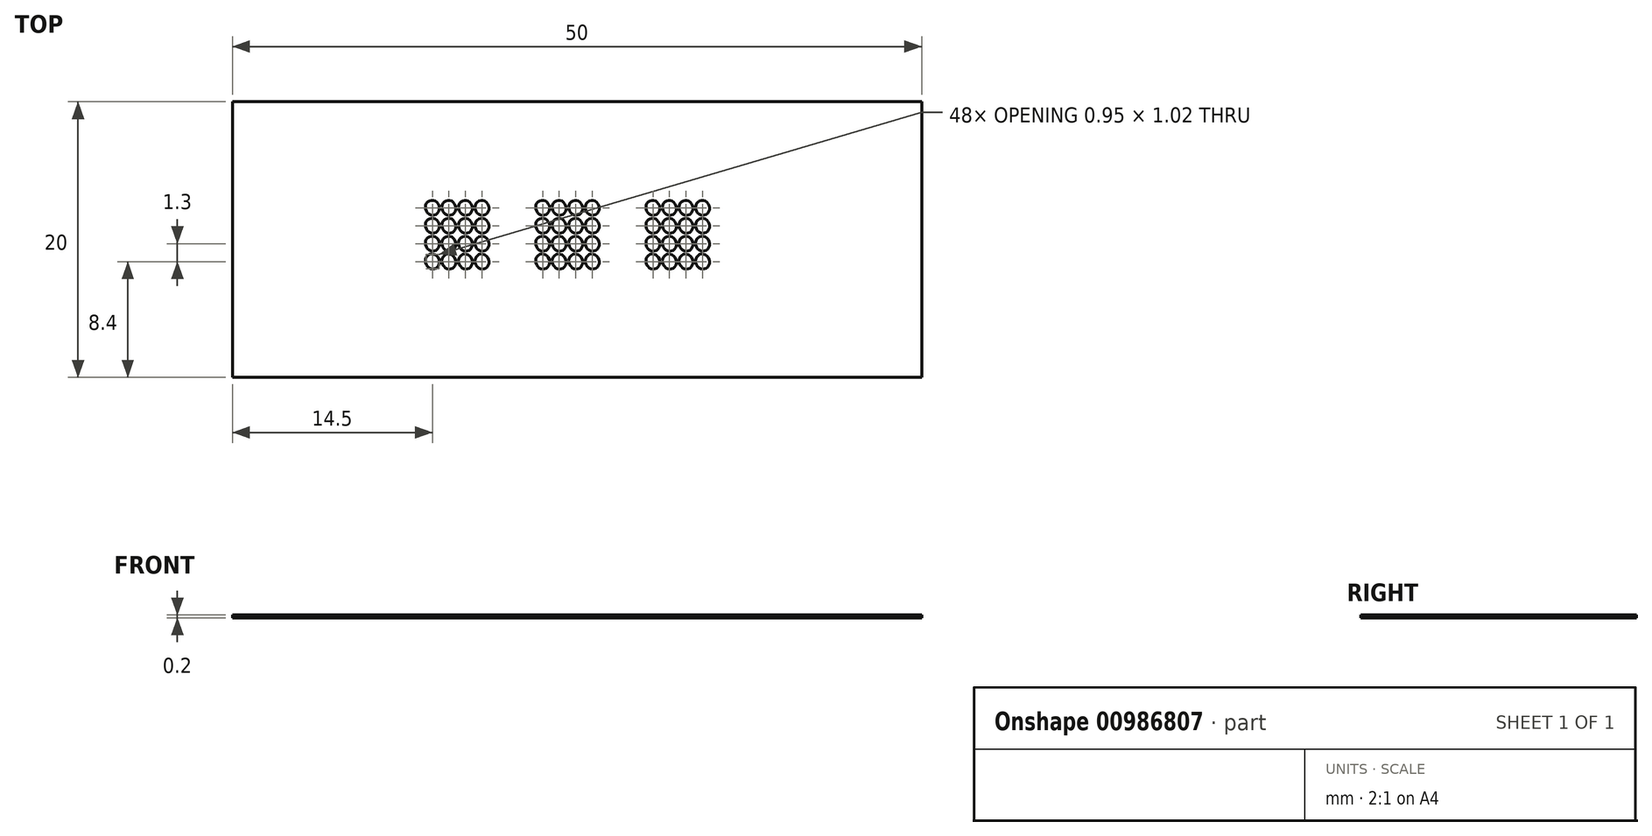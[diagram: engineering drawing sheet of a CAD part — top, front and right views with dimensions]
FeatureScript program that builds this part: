
annotation { "Feature Type Name" : "Feature", "Feature Type Description" : "" }
export const myFeature = defineFeature(function(context is Context, id is Id, definition is map)
    precondition{}
    {
        {
            var Q0;
            Q0=qCreatedBy(makeId("Top.planeOp"),FACE);
            var sketch = newSketch(context, id + "F0", { "sketchPlane" : qUnion([Q0])});
            skLineSegment(sketch, "E0.bottom", {"start": v(0, 0) * mm, "end": v(50, 0) * mm});
            skLineSegment(sketch, "E0.top", {"start": v(0, -20) * mm, "end": v(50, -20) * mm});
            skLineSegment(sketch, "E0.left", {"start": v(0, 0) * mm, "end": v(0, -20) * mm});
            skLineSegment(sketch, "E0.right", {"start": v(50, 0) * mm, "end": v(50, -20) * mm});
            skEllipse(sketch, "E1", {"center": v(14.5, -7.7) * mm, "majorRadius": 0.5 * mm, "minorRadius": 0.55 * mm, "majorAxis": v(0.93, 0.38)});
            skLineSegment(sketch, "E2.direction1", {"start": v(14.5, -7.7) * mm, "end": v(15.7, -7.7) * mm, "construction": true});
            skEllipse(sketch, "E3.0.1.0", {"center": v(15.7, -7.7) * mm, "majorRadius": 0.5 * mm, "minorRadius": 0.55 * mm, "majorAxis": v(0.93, 0.38)});
            skEllipse(sketch, "E3.0.2.0", {"center": v(16.9, -7.7) * mm, "majorRadius": 0.5 * mm, "minorRadius": 0.55 * mm, "majorAxis": v(0.93, 0.38)});
            skEllipse(sketch, "E3.0.3.0", {"center": v(18.1, -7.7) * mm, "majorRadius": 0.5 * mm, "minorRadius": 0.55 * mm, "majorAxis": v(0.93, 0.38)});
            skEllipse(sketch, "E4.1.0.0", {"center": v(15.7, -9) * mm, "majorRadius": 0.5 * mm, "minorRadius": 0.55 * mm, "majorAxis": v(0.93, 0.38)});
            skEllipse(sketch, "E4.1.0.1", {"center": v(14.5, -9) * mm, "majorRadius": 0.5 * mm, "minorRadius": 0.55 * mm, "majorAxis": v(0.93, 0.38)});
            skEllipse(sketch, "E4.1.0.2", {"center": v(18.1, -9) * mm, "majorRadius": 0.5 * mm, "minorRadius": 0.55 * mm, "majorAxis": v(0.93, 0.38)});
            skLineSegment(sketch, "E4.1.0.3", {"start": v(14.5, -9) * mm, "end": v(15.7, -9) * mm, "construction": true});
            skEllipse(sketch, "E4.1.0.4", {"center": v(16.9, -9) * mm, "majorRadius": 0.5 * mm, "minorRadius": 0.55 * mm, "majorAxis": v(0.93, 0.38)});
            skEllipse(sketch, "E4.2.0.0", {"center": v(15.7, -10.3) * mm, "majorRadius": 0.5 * mm, "minorRadius": 0.55 * mm, "majorAxis": v(0.93, 0.38)});
            skEllipse(sketch, "E4.2.0.1", {"center": v(14.5, -10.3) * mm, "majorRadius": 0.5 * mm, "minorRadius": 0.55 * mm, "majorAxis": v(0.93, 0.38)});
            skEllipse(sketch, "E4.2.0.2", {"center": v(18.1, -10.3) * mm, "majorRadius": 0.5 * mm, "minorRadius": 0.55 * mm, "majorAxis": v(0.93, 0.38)});
            skLineSegment(sketch, "E4.2.0.3", {"start": v(14.5, -10.3) * mm, "end": v(15.7, -10.3) * mm, "construction": true});
            skEllipse(sketch, "E4.2.0.4", {"center": v(16.9, -10.3) * mm, "majorRadius": 0.5 * mm, "minorRadius": 0.55 * mm, "majorAxis": v(0.93, 0.38)});
            skEllipse(sketch, "E4.3.0.0", {"center": v(15.7, -11.6) * mm, "majorRadius": 0.5 * mm, "minorRadius": 0.55 * mm, "majorAxis": v(0.93, 0.38)});
            skEllipse(sketch, "E4.3.0.1", {"center": v(14.5, -11.6) * mm, "majorRadius": 0.5 * mm, "minorRadius": 0.55 * mm, "majorAxis": v(0.93, 0.38)});
            skEllipse(sketch, "E4.3.0.2", {"center": v(18.1, -11.6) * mm, "majorRadius": 0.5 * mm, "minorRadius": 0.55 * mm, "majorAxis": v(0.93, 0.38)});
            skLineSegment(sketch, "E4.3.0.3", {"start": v(14.5, -11.6) * mm, "end": v(15.7, -11.6) * mm, "construction": true});
            skEllipse(sketch, "E4.3.0.4", {"center": v(16.9, -11.6) * mm, "majorRadius": 0.5 * mm, "minorRadius": 0.55 * mm, "majorAxis": v(0.93, 0.38)});
            skLineSegment(sketch, "E4.direction1", {"start": v(14.5, -7.7) * mm, "end": v(14.5, -9) * mm, "construction": true});
            skEllipse(sketch, "E5.1.0.0", {"center": v(22.5, -7.7) * mm, "majorRadius": 0.5 * mm, "minorRadius": 0.55 * mm, "majorAxis": v(0.93, 0.38)});
            skEllipse(sketch, "E5.1.0.1", {"center": v(24.9, -11.6) * mm, "majorRadius": 0.5 * mm, "minorRadius": 0.55 * mm, "majorAxis": v(0.93, 0.38)});
            skEllipse(sketch, "E5.1.0.2", {"center": v(23.7, -11.6) * mm, "majorRadius": 0.5 * mm, "minorRadius": 0.55 * mm, "majorAxis": v(0.93, 0.38)});
            skEllipse(sketch, "E5.1.0.3", {"center": v(22.5, -10.3) * mm, "majorRadius": 0.5 * mm, "minorRadius": 0.55 * mm, "majorAxis": v(0.93, 0.38)});
            skEllipse(sketch, "E5.1.0.4", {"center": v(22.5, -9) * mm, "majorRadius": 0.5 * mm, "minorRadius": 0.55 * mm, "majorAxis": v(0.93, 0.38)});
            skEllipse(sketch, "E5.1.0.5", {"center": v(22.5, -11.6) * mm, "majorRadius": 0.5 * mm, "minorRadius": 0.55 * mm, "majorAxis": v(0.93, 0.38)});
            skEllipse(sketch, "E5.1.0.6", {"center": v(26.1, -11.6) * mm, "majorRadius": 0.5 * mm, "minorRadius": 0.55 * mm, "majorAxis": v(0.93, 0.38)});
            skEllipse(sketch, "E5.1.0.7", {"center": v(26.1, -7.7) * mm, "majorRadius": 0.5 * mm, "minorRadius": 0.55 * mm, "majorAxis": v(0.93, 0.38)});
            skEllipse(sketch, "E5.1.0.8", {"center": v(24.9, -7.7) * mm, "majorRadius": 0.5 * mm, "minorRadius": 0.55 * mm, "majorAxis": v(0.93, 0.38)});
            skEllipse(sketch, "E5.1.0.9", {"center": v(26.1, -10.3) * mm, "majorRadius": 0.5 * mm, "minorRadius": 0.55 * mm, "majorAxis": v(0.93, 0.38)});
            skEllipse(sketch, "E5.1.0.10", {"center": v(24.9, -10.3) * mm, "majorRadius": 0.5 * mm, "minorRadius": 0.55 * mm, "majorAxis": v(0.93, 0.38)});
            skEllipse(sketch, "E5.1.0.11", {"center": v(26.1, -9) * mm, "majorRadius": 0.5 * mm, "minorRadius": 0.55 * mm, "majorAxis": v(0.93, 0.38)});
            skEllipse(sketch, "E5.1.0.12", {"center": v(24.9, -9) * mm, "majorRadius": 0.5 * mm, "minorRadius": 0.55 * mm, "majorAxis": v(0.93, 0.38)});
            skEllipse(sketch, "E5.1.0.13", {"center": v(23.7, -9) * mm, "majorRadius": 0.5 * mm, "minorRadius": 0.55 * mm, "majorAxis": v(0.93, 0.38)});
            skLineSegment(sketch, "E5.1.0.14", {"start": v(22.5, -7.7) * mm, "end": v(23.7, -7.7) * mm, "construction": true});
            skEllipse(sketch, "E5.1.0.15", {"center": v(23.7, -7.7) * mm, "majorRadius": 0.5 * mm, "minorRadius": 0.55 * mm, "majorAxis": v(0.93, 0.38)});
            skEllipse(sketch, "E5.1.0.16", {"center": v(23.7, -10.3) * mm, "majorRadius": 0.5 * mm, "minorRadius": 0.55 * mm, "majorAxis": v(0.93, 0.38)});
            skLineSegment(sketch, "E5.1.0.17", {"start": v(22.5, -9) * mm, "end": v(23.7, -9) * mm, "construction": true});
            skLineSegment(sketch, "E5.1.0.18", {"start": v(22.5, -11.6) * mm, "end": v(23.7, -11.6) * mm, "construction": true});
            skLineSegment(sketch, "E5.1.0.19", {"start": v(22.5, -10.3) * mm, "end": v(23.7, -10.3) * mm, "construction": true});
            skLineSegment(sketch, "E5.1.0.20", {"start": v(22.5, -7.7) * mm, "end": v(22.5, -9) * mm, "construction": true});
            skEllipse(sketch, "E5.2.0.0", {"center": v(30.5, -7.7) * mm, "majorRadius": 0.5 * mm, "minorRadius": 0.55 * mm, "majorAxis": v(0.93, 0.38)});
            skEllipse(sketch, "E5.2.0.1", {"center": v(32.9, -11.6) * mm, "majorRadius": 0.5 * mm, "minorRadius": 0.55 * mm, "majorAxis": v(0.93, 0.38)});
            skEllipse(sketch, "E5.2.0.2", {"center": v(31.7, -11.6) * mm, "majorRadius": 0.5 * mm, "minorRadius": 0.55 * mm, "majorAxis": v(0.93, 0.38)});
            skEllipse(sketch, "E5.2.0.3", {"center": v(30.5, -10.3) * mm, "majorRadius": 0.5 * mm, "minorRadius": 0.55 * mm, "majorAxis": v(0.93, 0.38)});
            skEllipse(sketch, "E5.2.0.4", {"center": v(30.5, -9) * mm, "majorRadius": 0.5 * mm, "minorRadius": 0.55 * mm, "majorAxis": v(0.93, 0.38)});
            skEllipse(sketch, "E5.2.0.5", {"center": v(30.5, -11.6) * mm, "majorRadius": 0.5 * mm, "minorRadius": 0.55 * mm, "majorAxis": v(0.93, 0.38)});
            skEllipse(sketch, "E5.2.0.6", {"center": v(34.1, -11.6) * mm, "majorRadius": 0.5 * mm, "minorRadius": 0.55 * mm, "majorAxis": v(0.93, 0.38)});
            skEllipse(sketch, "E5.2.0.7", {"center": v(34.1, -7.7) * mm, "majorRadius": 0.5 * mm, "minorRadius": 0.55 * mm, "majorAxis": v(0.93, 0.38)});
            skEllipse(sketch, "E5.2.0.8", {"center": v(32.9, -7.7) * mm, "majorRadius": 0.5 * mm, "minorRadius": 0.55 * mm, "majorAxis": v(0.93, 0.38)});
            skEllipse(sketch, "E5.2.0.9", {"center": v(34.1, -10.3) * mm, "majorRadius": 0.5 * mm, "minorRadius": 0.55 * mm, "majorAxis": v(0.93, 0.38)});
            skEllipse(sketch, "E5.2.0.10", {"center": v(32.9, -10.3) * mm, "majorRadius": 0.5 * mm, "minorRadius": 0.55 * mm, "majorAxis": v(0.93, 0.38)});
            skEllipse(sketch, "E5.2.0.11", {"center": v(34.1, -9) * mm, "majorRadius": 0.5 * mm, "minorRadius": 0.55 * mm, "majorAxis": v(0.93, 0.38)});
            skEllipse(sketch, "E5.2.0.12", {"center": v(32.9, -9) * mm, "majorRadius": 0.5 * mm, "minorRadius": 0.55 * mm, "majorAxis": v(0.93, 0.38)});
            skEllipse(sketch, "E5.2.0.13", {"center": v(31.7, -9) * mm, "majorRadius": 0.5 * mm, "minorRadius": 0.55 * mm, "majorAxis": v(0.93, 0.38)});
            skLineSegment(sketch, "E5.2.0.14", {"start": v(30.5, -7.7) * mm, "end": v(31.7, -7.7) * mm, "construction": true});
            skEllipse(sketch, "E5.2.0.15", {"center": v(31.7, -7.7) * mm, "majorRadius": 0.5 * mm, "minorRadius": 0.55 * mm, "majorAxis": v(0.93, 0.38)});
            skEllipse(sketch, "E5.2.0.16", {"center": v(31.7, -10.3) * mm, "majorRadius": 0.5 * mm, "minorRadius": 0.55 * mm, "majorAxis": v(0.93, 0.38)});
            skLineSegment(sketch, "E5.2.0.17", {"start": v(30.5, -9) * mm, "end": v(31.7, -9) * mm, "construction": true});
            skLineSegment(sketch, "E5.2.0.18", {"start": v(30.5, -11.6) * mm, "end": v(31.7, -11.6) * mm, "construction": true});
            skLineSegment(sketch, "E5.2.0.19", {"start": v(30.5, -10.3) * mm, "end": v(31.7, -10.3) * mm, "construction": true});
            skLineSegment(sketch, "E5.2.0.20", {"start": v(30.5, -7.7) * mm, "end": v(30.5, -9) * mm, "construction": true});
            skLineSegment(sketch, "E5.direction1", {"start": v(14.5, -11.6) * mm, "end": v(22.5, -11.6) * mm, "construction": true});
            skSolve(sketch);
        }
        {
            var Q0;
            Q0=makeQuery(id+"F0.imprint","IMPRINT",FACE,{"disambiguationData":[TD([[makeQuery(id+"F0.imprint","IMPRINT",EDGE,{"derivedFrom":sQuery(id+"F0.wireOp",EDGE,"E0.bottom")}),-1.0]])]});
            extrude(context, id + "F1", {"entities" : qUnion([Q0]), "depth" : 0.2 * mm, "offsetDistance" : 25.4 * mm});
        }
    });
